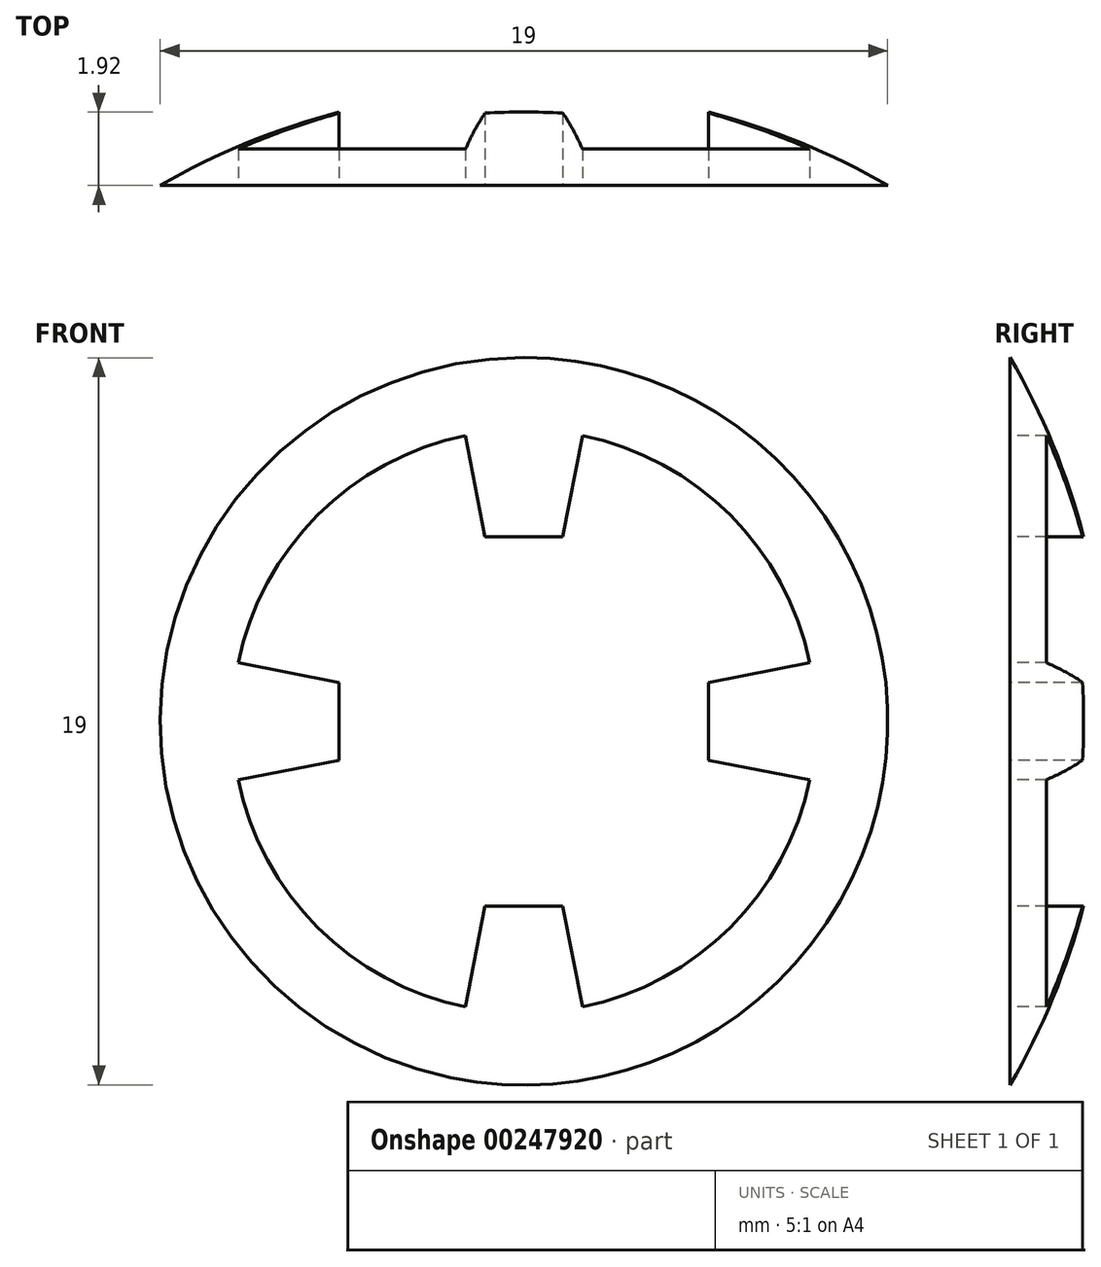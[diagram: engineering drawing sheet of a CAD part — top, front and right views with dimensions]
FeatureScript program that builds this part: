
annotation { "Feature Type Name" : "Feature", "Feature Type Description" : "" }
export const myFeature = defineFeature(function(context is Context, id is Id, definition is map)
    precondition{}
    {
        {
            var Q0;
            Q0=qCreatedBy(makeId("Right.planeOp"),FACE);
            var sketch = newSketch(context, id + "F0", { "sketchPlane" : qUnion([Q0])});
            skArc(sketch, "E0", {"start": v(19.05, 0) * mm, "mid": v(18.4, 4.92) * mm, "end": v(16.51, 9.5) * mm});
            skLineSegment(sketch, "E1", {"start": v(16.51, 0) * mm, "end": v(19.05, 0) * mm});
            skLineSegment(sketch, "E2", {"start": v(19.05, 0) * mm, "end": v(16.51, 0) * mm});
            skLineSegment(sketch, "E3", {"start": v(16.51, 0) * mm, "end": v(16.51, 9.5) * mm});
            skPoint(sketch, "E4.start.orphan", {"position": v(0, -19.05) * mm});
            skSolve(sketch);
        }
        {
            var Q0;
            Q0=makeQuery(id+"F0.imprint","IMPRINT",FACE,{"disambiguationData":[TD([[makeQuery(id+"F0.imprint","IMPRINT",EDGE,{"derivedFrom":sQuery(id+"F0.wireOp",EDGE,"E0")}),1.0]])]});
            var Q1;
            Q1=sQuery(id+"F0.wireOp",EDGE,"E2");
            revolve(context, id + "F1", {"entities" : qUnion([Q0]), "axis" : qUnion([Q1]), "revolveType" : RevolveType.FULL});
        }
        {
            var Q0;
            Q0=makeQuery(id+"F1.opRevolve","SWEPT_FACE",FACE,{"disambiguationData":[OSD([sQuery(id+"F0.wireOp",EDGE,"E3")])]});
            var sketch = newSketch(context, id + "F2", { "sketchPlane" : qUnion([Q0])});
            skCircle(sketch, "E5", {"center": v(0, 0) * mm, "radius": 10.67 * mm});
            skArc(sketch, "E6", {"start": v(1.53, -7.47) * mm, "mid": v(5.39, -5.39) * mm, "end": v(7.47, -1.53) * mm});
            skLineSegment(sketch, "E7", {"start": v(0, -4.83) * mm, "end": v(-1.02, -4.83) * mm});
            skLineSegment(sketch, "E8", {"start": v(-1.02, -4.83) * mm, "end": v(-1.53, -7.47) * mm});
            skLineSegment(sketch, "E9.MirrorCS", {"start": v(1.02, -4.83) * mm, "end": v(1.53, -7.47) * mm});
            skLineSegment(sketch, "E10.MirrorCS", {"start": v(0, -4.83) * mm, "end": v(1.02, -4.83) * mm});
            skLineSegment(sketch, "E11.1.0", {"start": v(4.83, -1.02) * mm, "end": v(7.47, -1.53) * mm});
            skLineSegment(sketch, "E11.1.1", {"start": v(4.83, 0) * mm, "end": v(4.83, 1.02) * mm});
            skLineSegment(sketch, "E11.1.2", {"start": v(4.83, 0) * mm, "end": v(4.83, -1.02) * mm});
            skLineSegment(sketch, "E11.1.3", {"start": v(4.83, 1.02) * mm, "end": v(7.47, 1.53) * mm});
            skLineSegment(sketch, "E11.2.0", {"start": v(1.02, 4.83) * mm, "end": v(1.53, 7.47) * mm});
            skLineSegment(sketch, "E11.2.1", {"start": v(0, 4.83) * mm, "end": v(-1.02, 4.83) * mm});
            skLineSegment(sketch, "E11.2.2", {"start": v(0, 4.83) * mm, "end": v(1.02, 4.83) * mm});
            skLineSegment(sketch, "E11.2.3", {"start": v(-1.02, 4.83) * mm, "end": v(-1.53, 7.47) * mm});
            skLineSegment(sketch, "E11.3.0", {"start": v(-4.83, 1.02) * mm, "end": v(-7.47, 1.53) * mm});
            skLineSegment(sketch, "E11.3.1", {"start": v(-4.83, 0) * mm, "end": v(-4.83, -1.02) * mm});
            skLineSegment(sketch, "E11.3.2", {"start": v(-4.83, 0) * mm, "end": v(-4.83, 1.02) * mm});
            skLineSegment(sketch, "E11.3.3", {"start": v(-4.83, -1.02) * mm, "end": v(-7.47, -1.53) * mm});
            skArc(sketch, "E12.trimOffspring", {"start": v(-7.47, -1.53) * mm, "mid": v(-5.39, -5.39) * mm, "end": v(-1.53, -7.47) * mm});
            skArc(sketch, "E13.trimOffspring", {"start": v(-1.53, 7.47) * mm, "mid": v(-5.39, 5.39) * mm, "end": v(-7.47, 1.53) * mm});
            skArc(sketch, "E14.trimOffspring", {"start": v(7.47, 1.53) * mm, "mid": v(5.39, 5.39) * mm, "end": v(1.53, 7.47) * mm});
            skSolve(sketch);
        }
        {
            var Q0;
            Q0=makeQuery(id+"F2.imprint","IMPRINT",FACE,{"disambiguationData":[TD([[makeQuery(id+"F2.imprint","IMPRINT",EDGE,{"derivedFrom":sQuery(id+"F2.wireOp",EDGE,"E6")}),1.0]])]});
            extrude(context, id + "F3", {"entities" : qUnion([Q0]), "operationType" : NewBodyOperationType.REMOVE, "endBound" : BoundingType.THROUGH_ALL, "oppositeDirection" : true, "depth" : 25.4 * mm});
        }
    });
